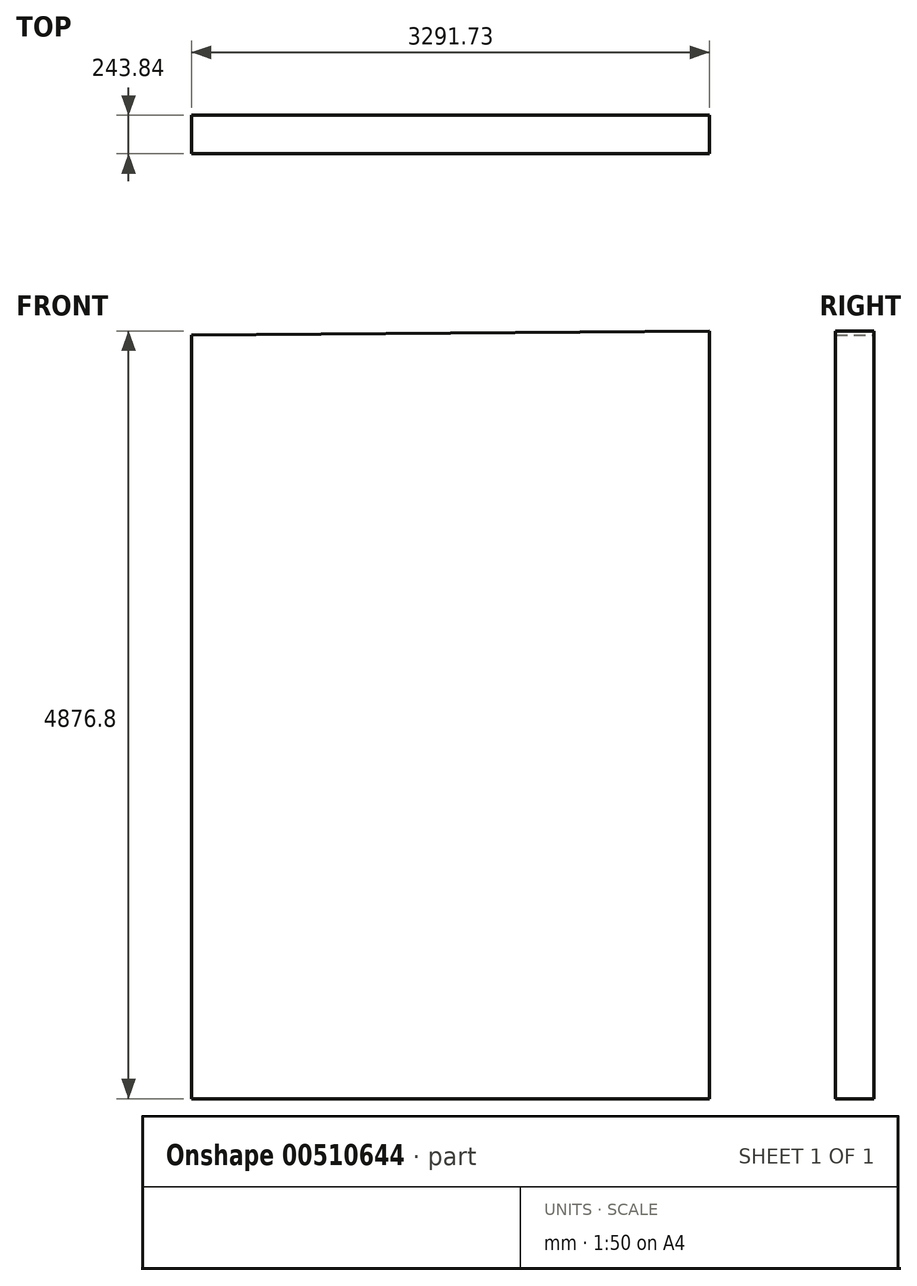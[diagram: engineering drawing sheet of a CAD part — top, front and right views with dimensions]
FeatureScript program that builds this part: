
annotation { "Feature Type Name" : "Feature", "Feature Type Description" : "" }
export const myFeature = defineFeature(function(context is Context, id is Id, definition is map)
    precondition{}
    {
        {
            var Q0;
            Q0=qCreatedBy(makeId("Front.planeOp"),FACE);
            var sketch = newSketch(context, id + "F0", { "sketchPlane" : qUnion([Q0])});
            skLineSegment(sketch, "E0", {"start": v(-1531.72, 806.3) * mm, "end": v(-1531.72, -4043.87) * mm});
            skLineSegment(sketch, "E1", {"start": v(-1531.72, -4043.87) * mm, "end": v(1760.01, -4043.87) * mm});
            skLineSegment(sketch, "E2", {"start": v(1760.01, -4043.87) * mm, "end": v(1760.01, 832.93) * mm});
            skLineSegment(sketch, "E3", {"start": v(1760.01, 832.93) * mm, "end": v(-1531.72, 806.3) * mm});
            skSolve(sketch);
        }
        {
            var Q0;
            Q0 = qSketchRegion(id + "F0", true);
            extrude(context, id + "F1", {"entities" : qUnion([Q0]), "depth" : 243.84 * mm, "offsetDistance" : 30.48 * mm});
        }
    });
